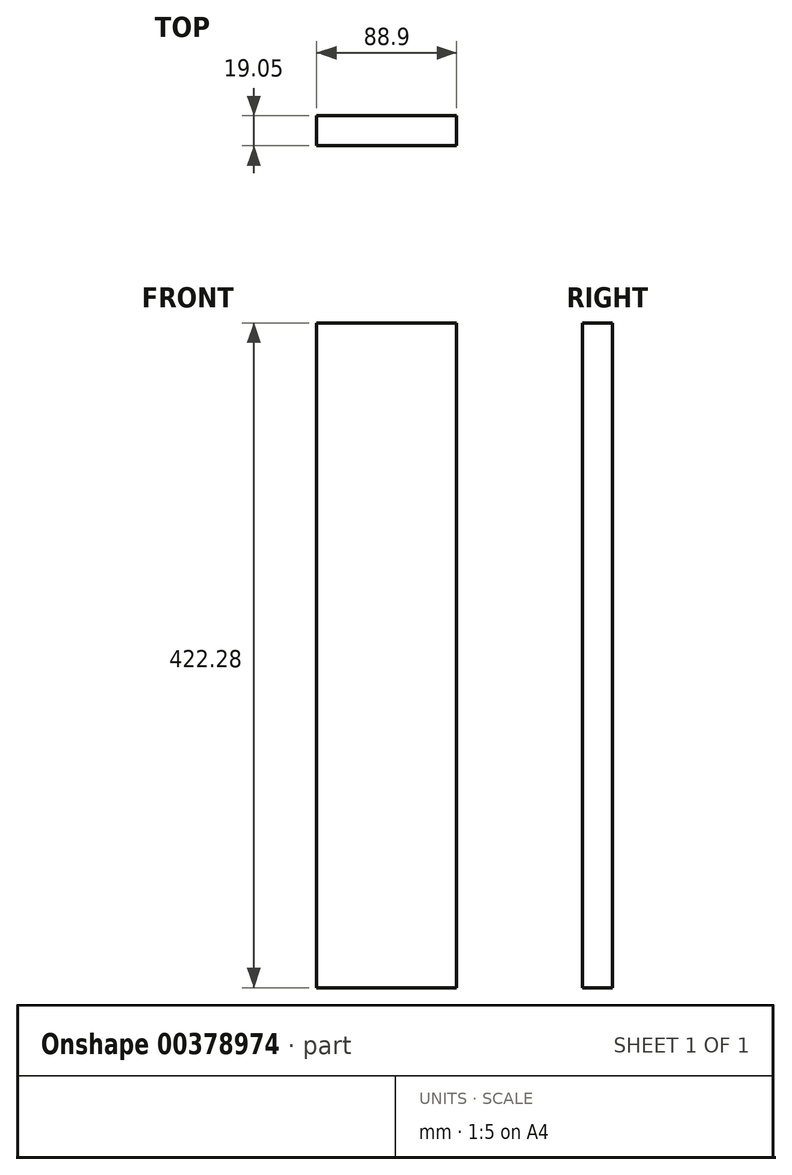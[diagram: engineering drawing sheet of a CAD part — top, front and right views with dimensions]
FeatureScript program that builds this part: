
annotation { "Feature Type Name" : "Feature", "Feature Type Description" : "" }
export const myFeature = defineFeature(function(context is Context, id is Id, definition is map)
    precondition{}
    {
        {
            var Q0;
            Q0=qCreatedBy(makeId("Front.planeOp"),FACE);
            var sketch = newSketch(context, id + "F0", { "sketchPlane" : qUnion([Q0])});
            skLineSegment(sketch, "E0.bottom", {"start": v(-75.75, 220.62) * mm, "end": v(13.15, 220.62) * mm});
            skLineSegment(sketch, "E0.top", {"start": v(-75.75, -201.66) * mm, "end": v(13.15, -201.66) * mm});
            skLineSegment(sketch, "E0.left", {"start": v(-75.75, 220.62) * mm, "end": v(-75.75, -201.66) * mm});
            skLineSegment(sketch, "E0.right", {"start": v(13.15, 220.62) * mm, "end": v(13.15, -201.66) * mm});
            skSolve(sketch);
        }
        {
            var Q0;
            Q0 = qSketchRegion(id + "F0", true);
            extrude(context, id + "F1", {"entities" : qUnion([Q0]), "depth" : 19.05 * mm, "offsetDistance" : 25.4 * mm});
        }
    });
